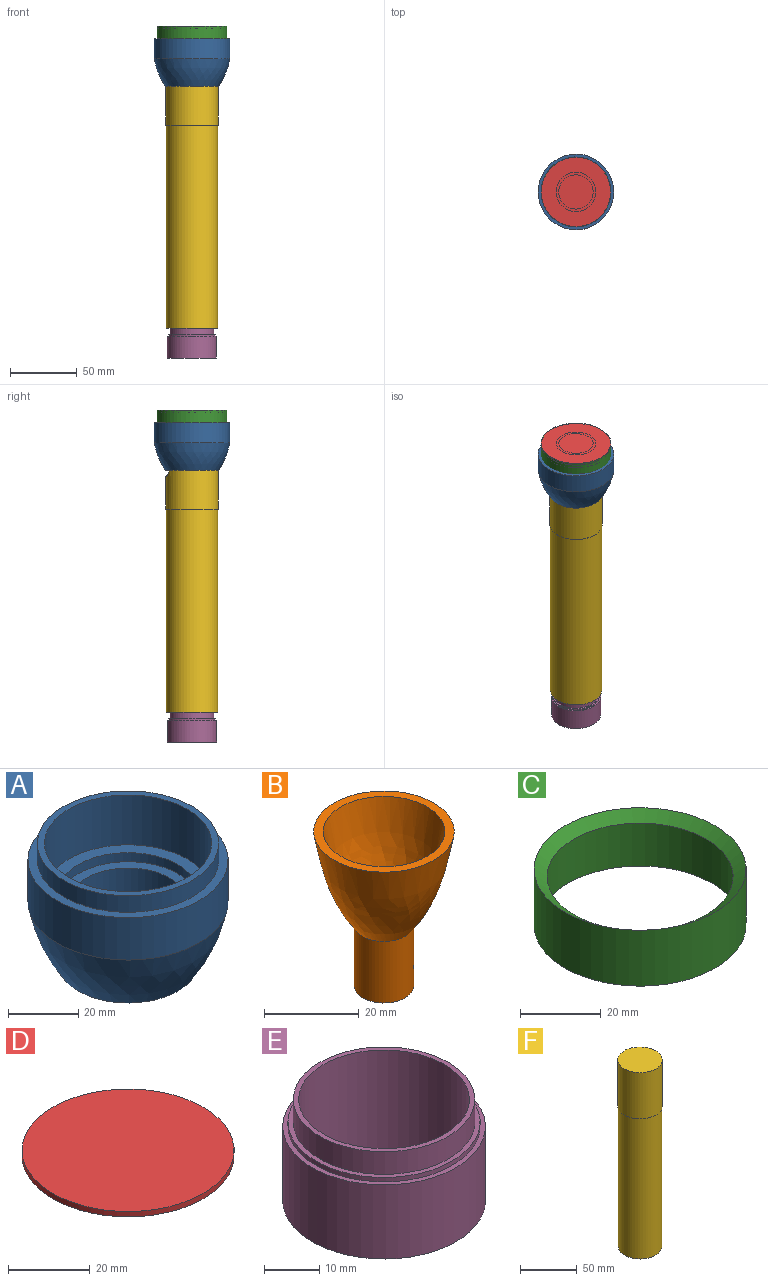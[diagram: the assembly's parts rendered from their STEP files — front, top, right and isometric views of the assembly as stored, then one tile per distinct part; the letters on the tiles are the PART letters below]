
ASSEMBLY  parts=6 mates=5
PART A: 12 faces, bbox 56.8x56.8x41.4 mm
  f0: cylinder r=19.89mm len=39.78mm, axis (0,0,1), area 392.4mm2, adj f1,f11
  f1: plane 39.78x39.78mm, normal (0,0,1), area 361.6mm2, adj f0,f2
  f2: cylinder r=16.75mm len=33.5mm, axis (0,0,1), area 1157.7mm2, adj f1,f3
  f3: plane 39.78x39.78mm, normal (0,0,-1), area 361.6mm2, adj f2,f4
  f4: cylinder r=19.89mm len=39.78mm, axis (0,0,1), area 1249.8mm2, adj f3,f5
  f5: revolved ~56.83x56.83mm, area 3563.5mm2, adj f4,f6
  f6: cylinder r=28.41mm len=56.83mm, axis (0,0,1), area 2630.1mm2, adj f5,f7
  f7: plane 56.83x56.83mm, normal (0,0,1), area 453mm2, adj f6,f8
  f8: cylinder r=25.75mm len=51.5mm, axis (0,0,1), area 933.1mm2, adj f7,f9
  f9: plane 51.5x51.5mm, normal (0,0,1), area 311mm2, adj f8,f10
  f10: cylinder r=23.75mm len=47.5mm, axis (0,0,1), area 2581.7mm2, adj f9,f11
  f11: plane 47.5x47.5mm, normal (0,0,1), area 529.1mm2, adj f0,f10
PART B: 6 faces, bbox 29.7x29.7x39.9 mm
  f0: cylinder r=6.25mm len=15.91mm, axis (0,0,-1), area 624.7mm2, adj f1,f5
  f1: revolved ~29.68x29.68mm, area 1863.4mm2, adj f0,f2
  f2: plane 29.68x29.68mm, normal (0,0,1), area 173.9mm2, adj f1,f3
  f3: revolved ~25.68x25.68mm, area 1539.8mm2, adj f2,f4
  f4: cylinder r=4.25mm len=15.91mm, axis (0,0,-1), area 424.8mm2, adj f3,f5
  f5: plane 12.5x12.5mm, normal (0,0,-1), area 66mm2, adj f0,f4
PART C: 5 faces, bbox 52.5x52.5x16.9 mm
  f0: cylinder r=26.25mm len=52.5mm, axis (0,0,1), area 2795.2mm2, adj f1,f4
  f1: cone r=26.25mm half-angle=53.1deg, axis (0,0,1), area 619.5mm2, adj f0,f2
  f2: plane 50.5x50.5mm, normal (0,0,-1), area 333.8mm2, adj f1,f3
  f3: cylinder r=25.25mm len=50.5mm, axis (0,0,1), area 2308mm2, adj f2,f4
  f4: plane 52.5x52.5mm, normal (0,0,-1), area 161.8mm2, adj f0,f3
PART D: 3 faces, bbox 52x52x1.6 mm
  f0: cylinder r=26mm len=52mm, axis (0,0,-1), area 261.4mm2, adj f1,f2
  f1: plane 52x52mm, normal (0,0,1), area 2123.7mm2, adj f0
  f2: plane 52x52mm, normal (0,0,-1), area 2123.7mm2, adj f0
PART E: 8 faces, bbox 36.8x36.8x22.5 mm
  f0: plane 32.94x32.94mm, normal (0,0,1), area 97.3mm2, adj f1,f7
  f1: cylinder r=15.5mm len=31mm, axis (0,0,1), area 2188.7mm2, adj f0,f2
  f2: plane 36.81x36.81mm, normal (0,0,-1), area 309.6mm2, adj f1,f3
  f3: cylinder r=18.41mm len=36.81mm, axis (0,0,1), area 1904.5mm2, adj f2,f4
  f4: plane 36.81x36.81mm, normal (0,0,1), area 109.1mm2, adj f3,f5
  f5: cylinder r=17.44mm len=34.88mm, axis (0,0,1), area 106.1mm2, adj f4,f6
  f6: plane 34.88x34.88mm, normal (0,0,1), area 103.2mm2, adj f5,f7
  f7: cylinder r=16.47mm len=32.94mm, axis (0,0,1), area 521.2mm2, adj f0,f6
PART F: 6 faces, bbox 39.4x39.4x202.3 mm
  f0: cylinder r=19.7mm len=50mm, axis (0,0,-1), area 5829.3mm2, adj f1,f2,f5
  f1: plane 39.4x39.4mm, normal (0,0,1), area 1219.2mm2, adj f0
  f2: plane 39.4x39.4mm, normal (0,0,-1), area 61.1mm2, adj f0,f3
  f3: cylinder r=19.2mm len=152.3mm, axis (0,0,1), area 18373mm2, adj f2,f4
  f4: plane 38.4x38.4mm, normal (0,0,-1), area 1158.1mm2, adj f3
  f5: extruded ~22.24x17.98mm, area 370.9mm2, adj f0
PLACE A t=(-3.84,20.56,-17.3)mm
PLACE B t=(-3.84,1.11,2.45)mm
PLACE C t=(-3.84,70.7,2.7)mm
PLACE D t=(29.79,-10.28,49.96)mm
PLACE E t=(-3.84,68.94,-223.85)mm
PLACE F t=(-3.84,20.56,-22.79)mm
MATE revolute D.f0 <-> C.f0  axis (0,0,1) through (-3.84,20.56,51.56)mm
MATE fastened B.f0 <-> C.f0  axis (0,0,-1) through (-3.84,20.56,51.56)mm
MATE revolute C.f0 <-> A.f0  axis (0,0,1) through (-3.84,20.56,41.88)mm
MATE fastened E.f1 <-> F.f3  axis (0,0,1) through (-3.84,20.56,-175.09)mm
MATE revolute F.f0 <-> A.f0  axis (0,0,1) through (-3.84,20.56,27.21)mm
